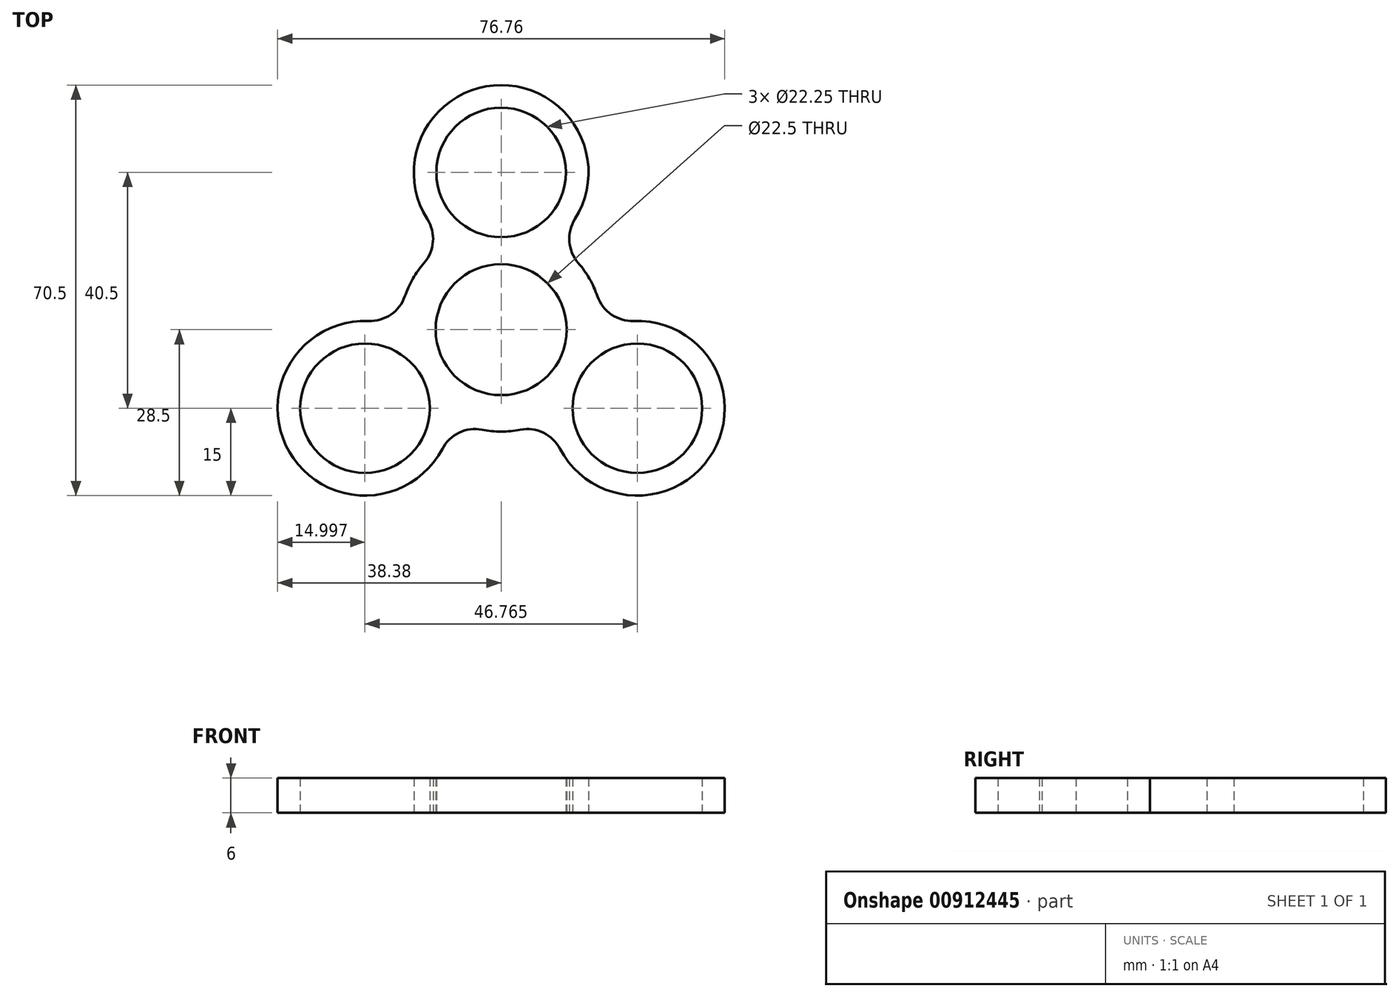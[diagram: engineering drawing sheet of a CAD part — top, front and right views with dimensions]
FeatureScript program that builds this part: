
annotation { "Feature Type Name" : "Feature", "Feature Type Description" : "" }
export const myFeature = defineFeature(function(context is Context, id is Id, definition is map)
    precondition{}
    {
        {
            var Q0;
            Q0=qCreatedBy(makeId("Top.planeOp"),FACE);
            var sketch = newSketch(context, id + "F0", { "sketchPlane" : qUnion([Q0])});
            skCircle(sketch, "E0", {"center": v(0, 0) * mm, "radius": 11.25 * mm});
            skArc(sketch, "E1", {"start": v(-13.24, 11.44) * mm, "mid": v(-15.16, 8.75) * mm, "end": v(-16.53, 5.75) * mm});
            skLineSegment(sketch, "E2", {"start": v(0, 11.25) * mm, "end": v(0, 12) * mm});
            skCircle(sketch, "E3", {"center": v(0, 27) * mm, "radius": 11.12 * mm});
            skLineSegment(sketch, "E4", {"start": v(-9.74, -5.62) * mm, "end": v(-10.4, -6) * mm});
            skCircle(sketch, "E5", {"center": v(-23.38, -13.5) * mm, "radius": 11.12 * mm});
            skArc(sketch, "E6", {"start": v(12.68, 18.99) * mm, "mid": v(0, 42) * mm, "end": v(-12.68, 18.99) * mm});
            skArc(sketch, "E7", {"start": v(-22.78, 1.49) * mm, "mid": v(-36.37, -21) * mm, "end": v(-10.1, -20.47) * mm});
            skCircle(sketch, "E8", {"center": v(23.38, -13.5) * mm, "radius": 11.12 * mm});
            skArc(sketch, "E9", {"start": v(10.1, -20.47) * mm, "mid": v(36.37, -21) * mm, "end": v(22.78, 1.49) * mm});
            skArc(sketch, "E10.trimOffspring", {"start": v(-3.29, -17.19) * mm, "mid": v(0, -17.5) * mm, "end": v(3.29, -17.19) * mm});
            skArc(sketch, "E11.trimOffspring", {"start": v(16.53, 5.75) * mm, "mid": v(15.16, 8.75) * mm, "end": v(13.24, 11.44) * mm});
            skPoint(sketch, "E12.visualSharp", {"position": v(17.5, 0.3) * mm});
            skArc(sketch, "E12.filletArc", {"start": v(16.53, 5.75) * mm, "mid": v(18.95, 2.58) * mm, "end": v(22.78, 1.49) * mm});
            skPoint(sketch, "E13.visualSharp", {"position": v(9, 15) * mm});
            skArc(sketch, "E13.filletArc", {"start": v(12.68, 18.99) * mm, "mid": v(11.71, 15.12) * mm, "end": v(13.24, 11.44) * mm});
            skPoint(sketch, "E14.visualSharp", {"position": v(-9, 15) * mm});
            skArc(sketch, "E14.filletArc", {"start": v(-13.24, 11.44) * mm, "mid": v(-11.71, 15.12) * mm, "end": v(-12.68, 18.99) * mm});
            skPoint(sketch, "E15.visualSharp", {"position": v(-17.5, 0.3) * mm});
            skArc(sketch, "E15.filletArc", {"start": v(-22.78, 1.49) * mm, "mid": v(-18.95, 2.58) * mm, "end": v(-16.53, 5.75) * mm});
            skPoint(sketch, "E16.visualSharp", {"position": v(-8.5, -15.3) * mm});
            skArc(sketch, "E16.filletArc", {"start": v(-3.29, -17.19) * mm, "mid": v(-7.24, -17.7) * mm, "end": v(-10.1, -20.47) * mm});
            skPoint(sketch, "E17.visualSharp", {"position": v(8.5, -15.3) * mm});
            skArc(sketch, "E17.filletArc", {"start": v(10.1, -20.47) * mm, "mid": v(7.24, -17.7) * mm, "end": v(3.29, -17.19) * mm});
            skSolve(sketch);
        }
        {
            var Q0;
            Q0=qSketchRegion(id+"F0",true);
            extrude(context, id + "F1", {"entities" : qUnion([Q0]), "depth" : 6 * mm, "offsetDistance" : 25.4 * mm});
        }
    });
